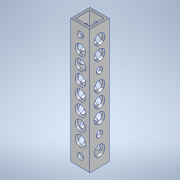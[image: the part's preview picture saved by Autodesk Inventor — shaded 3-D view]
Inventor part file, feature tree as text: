
AUTODESK INVENTOR PART (.ipt)
format: ipt  version: 2020.3 (Build 243373000, 373)  size: 215,552 bytes
history: native  units: mm
features: sketch x5, hole x4, other x1, extrude x1
ambient origin geometry x8: Origin, YZ Plane, XZ Plane, XY Plane, X Axis, Y Axis, Z Axis, Center Point
bodies: Body1 (feature_tree)
feature tree (11):
  other  "ソリッド1"
  extrude  "押し出し1"  Depth=9.0mm
  hole  "穴1"  [1 undecoded]
  hole  "穴2"  [1 undecoded]
  hole  "穴3"  [1 undecoded]
  hole  "穴4"  [1 undecoded]
  sketch  "スケッチ1"
  sketch  "スケッチ2"
  sketch  "スケッチ3"
  sketch  "スケッチ4"
  sketch  "スケッチ5"
note: 4 required parameter values undecoded (feature->parameter linkage not recoverable at this tier; creation-order binding heuristic only, values carry confidence <= 0.55)
